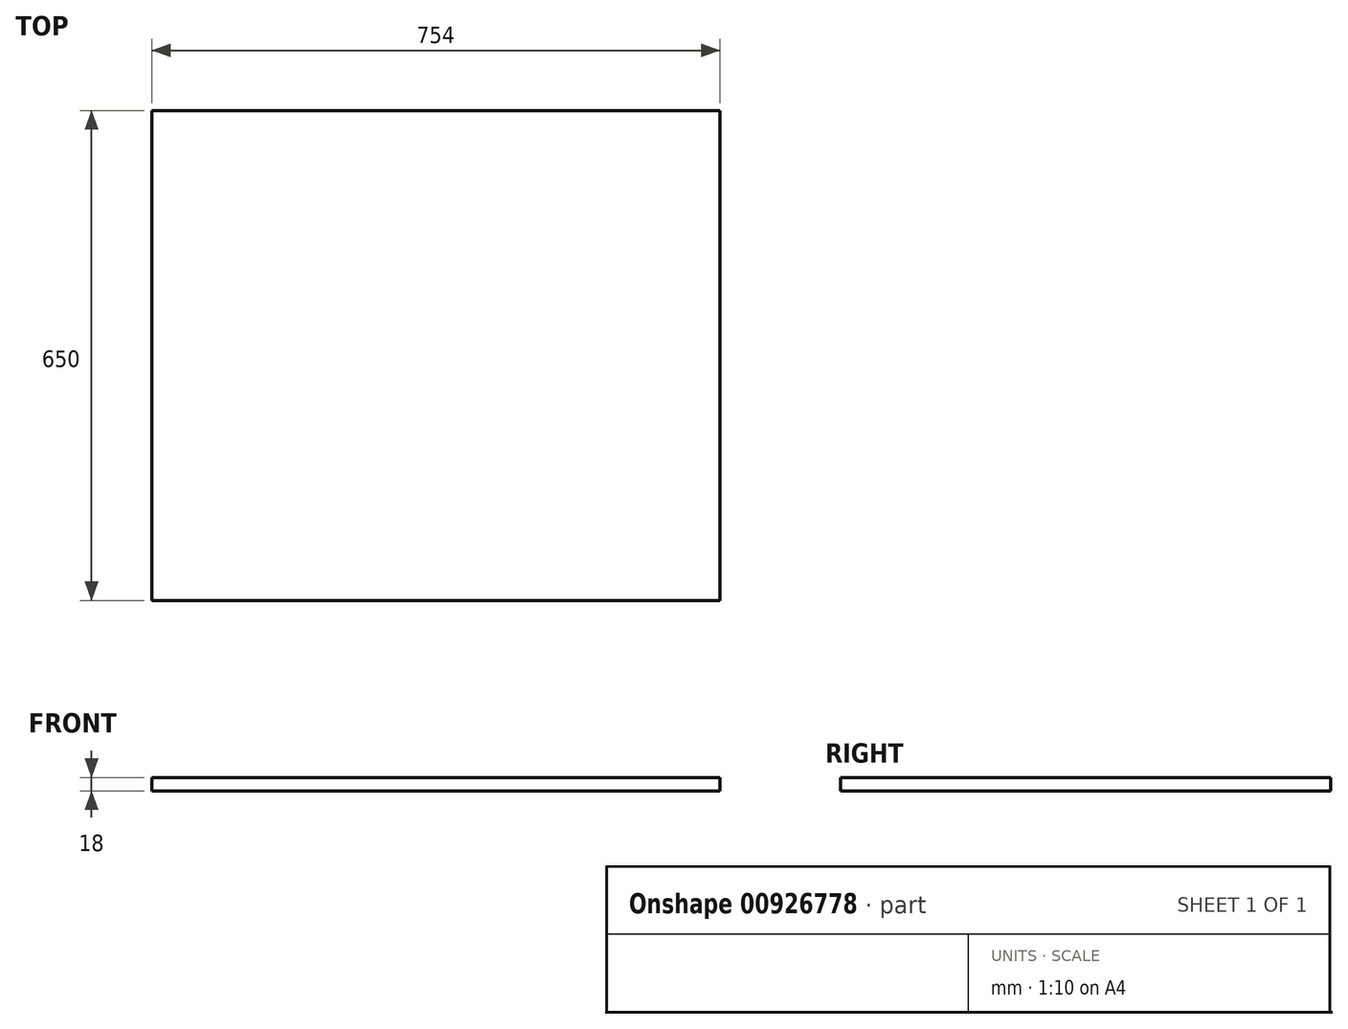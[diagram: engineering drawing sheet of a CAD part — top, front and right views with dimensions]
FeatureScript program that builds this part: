
annotation { "Feature Type Name" : "Feature", "Feature Type Description" : "" }
export const myFeature = defineFeature(function(context is Context, id is Id, definition is map)
    precondition{}
    {
        {
            var Q0;
            Q0=qCreatedBy(makeId("Top.planeOp"),FACE);
            var sketch = newSketch(context, id + "F0", { "sketchPlane" : qUnion([Q0])});
            skLineSegment(sketch, "E0.bottom", {"start": v(377, -325) * mm, "end": v(-377, -325) * mm});
            skLineSegment(sketch, "E0.top", {"start": v(377, 325) * mm, "end": v(-377, 325) * mm});
            skLineSegment(sketch, "E0.left", {"start": v(377, -325) * mm, "end": v(377, 325) * mm});
            skLineSegment(sketch, "E0.right", {"start": v(-377, -325) * mm, "end": v(-377, 325) * mm});
            skPoint(sketch, "E0.middle", {"position": v(0, 0) * mm});
            skSolve(sketch);
        }
        {
            var Q0;
            Q0 = qSketchRegion(id + "F0", true);
            extrude(context, id + "F1", {"entities" : qUnion([Q0]), "endBound" : BoundingType.SYMMETRIC, "depth" : 18 * mm, "offsetDistance" : 25 * mm});
        }
    });
